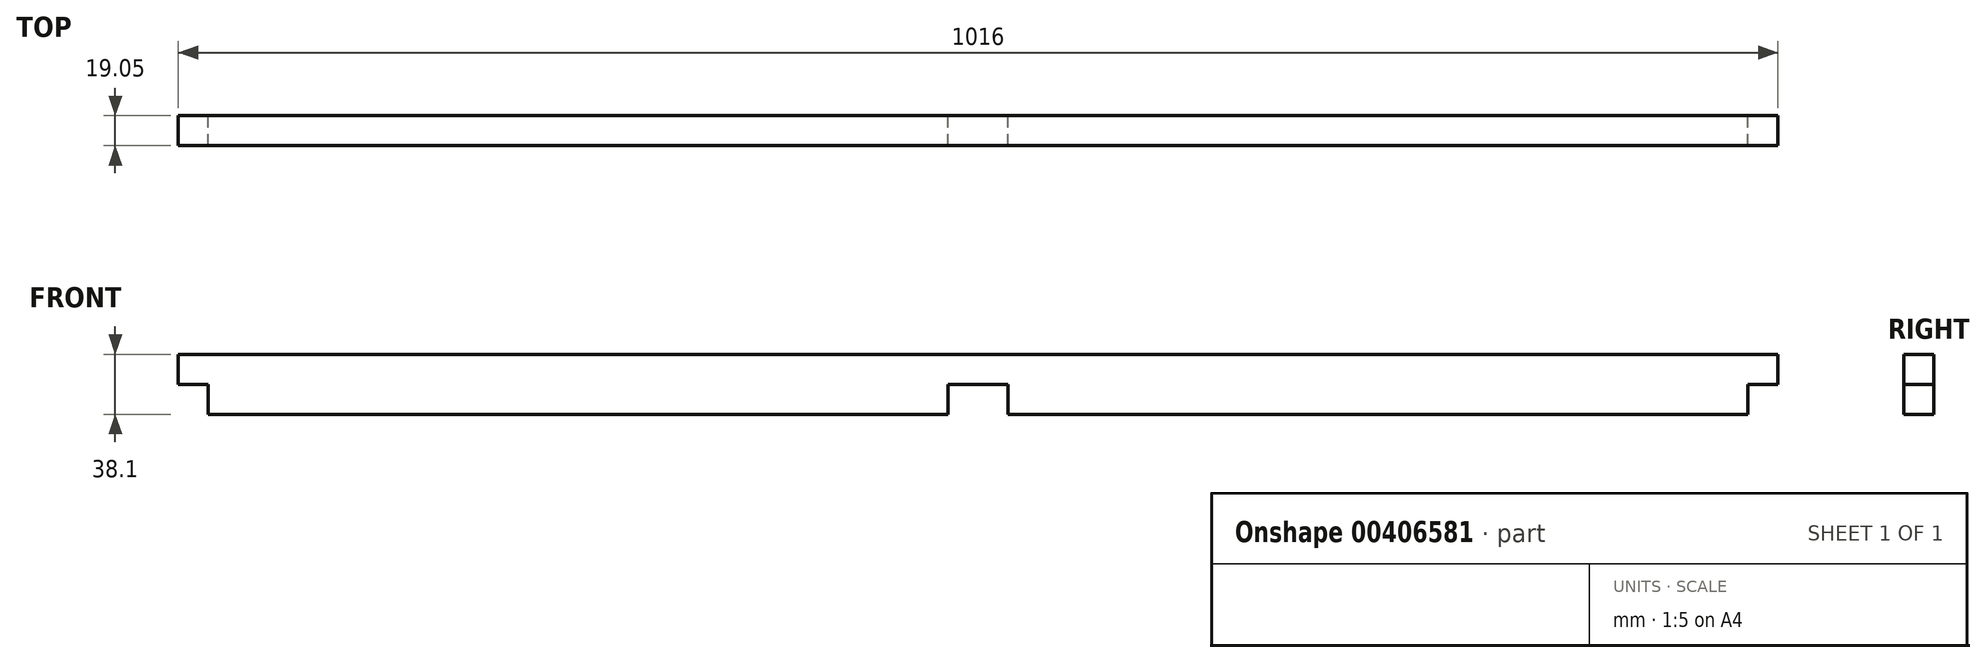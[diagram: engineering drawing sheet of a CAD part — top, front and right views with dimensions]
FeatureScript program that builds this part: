
annotation { "Feature Type Name" : "Feature", "Feature Type Description" : "" }
export const myFeature = defineFeature(function(context is Context, id is Id, definition is map)
    precondition{}
    {
        {
            var Q0;
            Q0=qCreatedBy(makeId("Front.planeOp"),FACE);
            var sketch = newSketch(context, id + "F0", { "sketchPlane" : qUnion([Q0])});
            skLineSegment(sketch, "E0", {"start": v(0, 0) * mm, "end": v(1016, 0) * mm});
            skLineSegment(sketch, "E1", {"start": v(1016, 0) * mm, "end": v(1016, -19.05) * mm});
            skLineSegment(sketch, "E2", {"start": v(1016, -19.05) * mm, "end": v(996.95, -19.05) * mm});
            skLineSegment(sketch, "E3", {"start": v(996.95, -19.05) * mm, "end": v(996.95, -38.1) * mm});
            skLineSegment(sketch, "E4", {"start": v(996.95, -38.1) * mm, "end": v(527.05, -38.1) * mm});
            skLineSegment(sketch, "E5", {"start": v(527.05, -38.1) * mm, "end": v(527.05, -19.05) * mm});
            skLineSegment(sketch, "E6", {"start": v(527.05, -19.05) * mm, "end": v(488.95, -19.05) * mm});
            skLineSegment(sketch, "E7", {"start": v(488.95, -19.05) * mm, "end": v(488.95, -38.1) * mm});
            skLineSegment(sketch, "E8", {"start": v(488.95, -38.1) * mm, "end": v(19.05, -38.1) * mm});
            skLineSegment(sketch, "E9", {"start": v(19.05, -38.1) * mm, "end": v(19.05, -19.05) * mm});
            skLineSegment(sketch, "E10", {"start": v(19.05, -19.05) * mm, "end": v(0, -19.05) * mm});
            skLineSegment(sketch, "E11", {"start": v(0, -19.05) * mm, "end": v(0, 0) * mm});
            skSolve(sketch);
        }
        {
            var Q0;
            Q0=makeQuery(id+"F0.imprint","IMPRINT",FACE,{"disambiguationData":[TD([[makeQuery(id+"F0.imprint","IMPRINT",EDGE,{"derivedFrom":sQuery(id+"F0.wireOp",EDGE,"E0")}),-1.0]])]});
            extrude(context, id + "F1", {"entities" : qUnion([Q0]), "depth" : 19.05 * mm});
        }
    });
